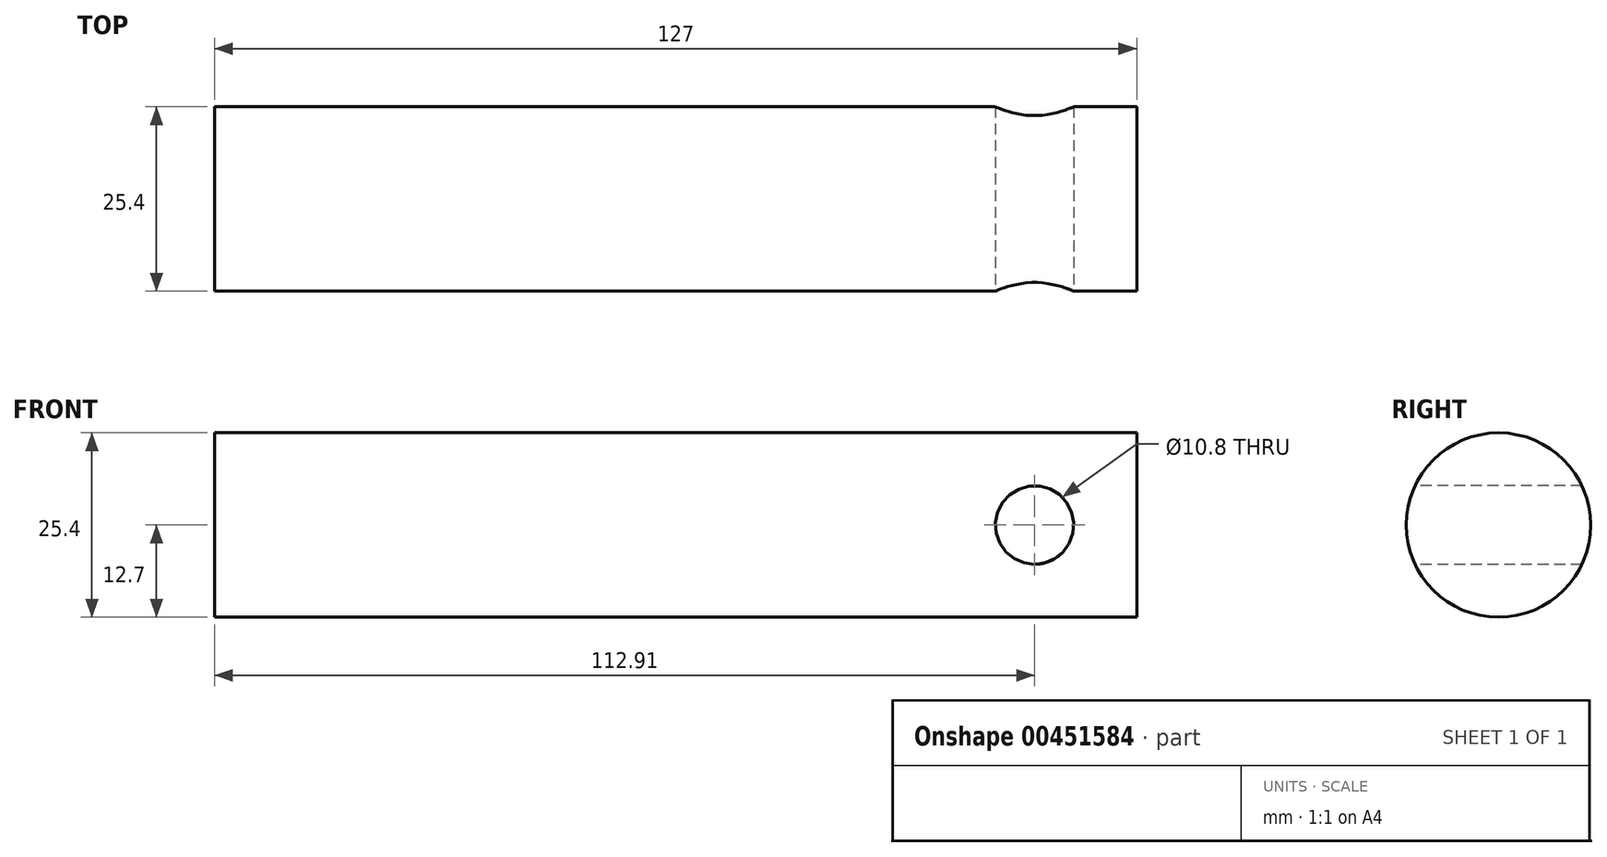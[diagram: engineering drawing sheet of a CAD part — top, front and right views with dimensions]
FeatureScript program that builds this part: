
annotation { "Feature Type Name" : "Feature", "Feature Type Description" : "" }
export const myFeature = defineFeature(function(context is Context, id is Id, definition is map)
    precondition{}
    {
        {
            var Q0;
            Q0=qCreatedBy(makeId("Right.planeOp"),FACE);
            var sketch = newSketch(context, id + "F0", { "sketchPlane" : qUnion([Q0])});
            skCircle(sketch, "E0", {"center": v(0, 0) * mm, "radius": 12.7 * mm});
            skSolve(sketch);
        }
        {
            var Q0;
            Q0 = qSketchRegion(id + "F0", true);
            extrude(context, id + "F1", {"entities" : qUnion([Q0]), "endBound" : BoundingType.SYMMETRIC, "depth" : 127 * mm});
        }
        {
            var Q0;
            Q0=qCreatedBy(makeId("Front.planeOp"),FACE);
            var sketch = newSketch(context, id + "F2", { "sketchPlane" : qUnion([Q0])});
            skCircle(sketch, "E1", {"center": v(49.41, 0) * mm, "radius": 5.4 * mm});
            skSolve(sketch);
        }
        {
            var Q0;
            Q0 = qSketchRegion(id + "F2", true);
            extrude(context, id + "F3", {"entities" : qUnion([Q0]), "operationType" : NewBodyOperationType.REMOVE, "endBound" : BoundingType.SYMMETRIC, "oppositeDirection" : true, "depth" : 48.26 * mm});
        }
    });
